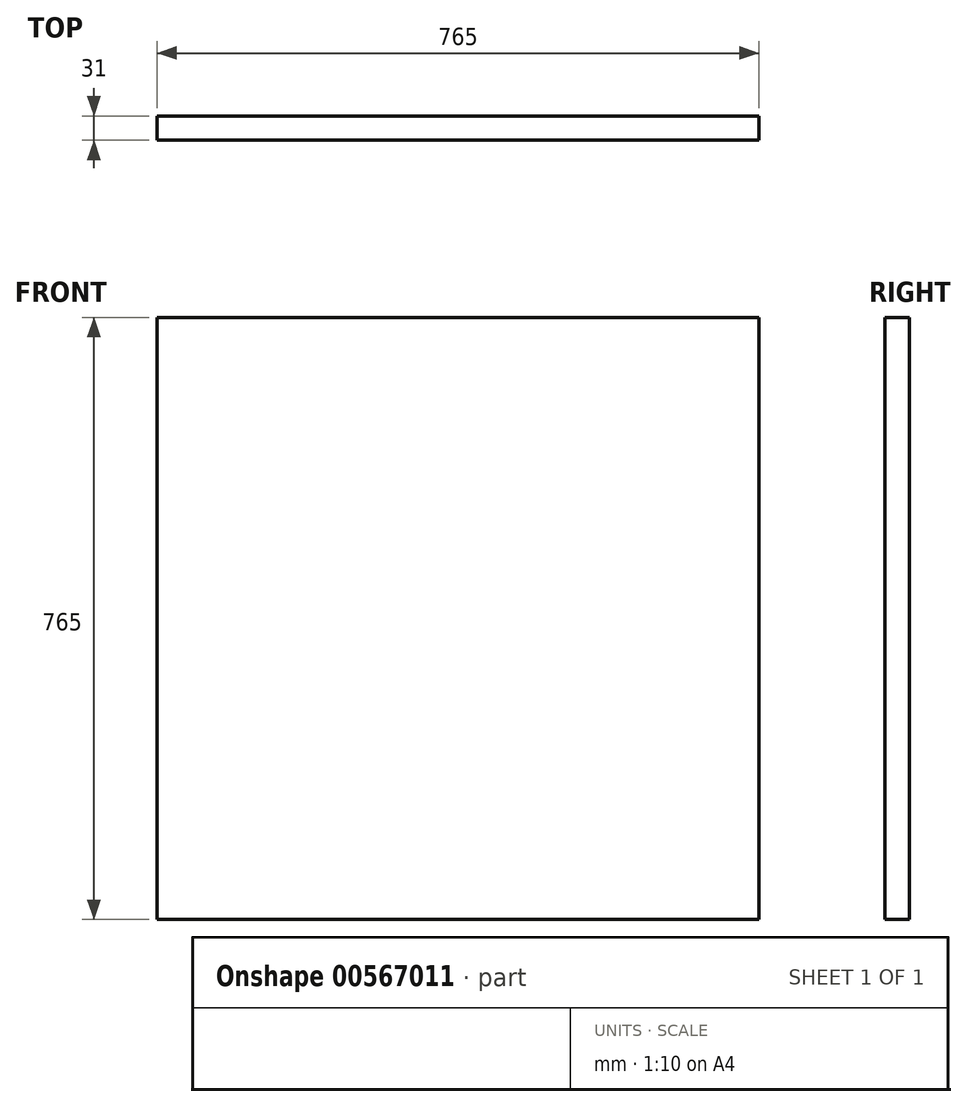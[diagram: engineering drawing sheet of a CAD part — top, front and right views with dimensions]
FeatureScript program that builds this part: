
annotation { "Feature Type Name" : "Feature", "Feature Type Description" : "" }
export const myFeature = defineFeature(function(context is Context, id is Id, definition is map)
    precondition{}
    {
        {
            var Q0;
            Q0=qCreatedBy(makeId("Front.planeOp"),FACE);
            var sketch = newSketch(context, id + "F0", { "sketchPlane" : qUnion([Q0])});
            skLineSegment(sketch, "E0.bottom", {"start": v(-756.96, 438.5) * mm, "end": v(8.04, 438.5) * mm});
            skLineSegment(sketch, "E0.top", {"start": v(-756.96, -326.5) * mm, "end": v(8.04, -326.5) * mm});
            skLineSegment(sketch, "E0.left", {"start": v(-756.96, 438.5) * mm, "end": v(-756.96, -326.5) * mm});
            skLineSegment(sketch, "E0.right", {"start": v(8.04, 438.5) * mm, "end": v(8.04, -326.5) * mm});
            skSolve(sketch);
        }
        {
            var Q0;
            Q0 = qSketchRegion(id + "F0", true);
            extrude(context, id + "F1", {"entities" : qUnion([Q0]), "depth" : 31 * mm, "offsetDistance" : 25 * mm});
        }
    });
